# Revit family: QF_ELECTROLUXPROFESSIONAL_1LSNBN_IC64832LF_E
name_source: partatom
category: Attrezzature speciali
units: mm (PartAtom-declared; Revit-internal decimal feet)

## family parameters
Basato su piano di lavoro = No
Condiviso = No
Punto di calcolo locali = No
Quota connettore circolare = Usa diametro
Sempre verticale = Sì
Taglio con vuoti quando caricato = No
Tipo di parte = Normale

## types (14) — shared parameters
Cycle = 50 Hz
Depth Actual = 1110 mm
Height Actual = 1270 mm  [stored 4.16667 ft]
Latent Heat Output = 0.0
Length Actual = 3835 mm
Modello = IC64832LF
Phase = 3
Produttore = Electrolux Professional
Sensible Heat Output = 0.0
URL = www.electroluxprofessional.com
Volts = 400 V
Weight = 1015
zero-valued in all types: Gas KW, Prospetto di default, Steam Pounds per Hour

## per-type parameters (varying)
| type | Descrizione | Item Number | Watts |
| 9882030112 | IRONER CYLINDER IC64832LF LENGTH FOLDING 3170MM ACTIVE EL. CE 400/50/3 6MM SST CYL. SE, DK, FI FEED NOW | 1L0GL8 | 56750 W |
| 9882030140 | IRONER CYLINDER IC64832LF LENGTH FOLDING 3170MM PERFORMANCE EL. CE 400/50/3 DUBIXIUM ML VAC.FEED.TABLE DIAMMS | 1L0GR3 | 56750 W |
| 9882030048 | IRONER CYLINDER IC64832LF LENGTH FOLDING 3170MM EL. CE 400/50/3 6MM SST CYL. FR FEED ALONE VAC.FEED.TABLE DIAMMS | 1LSP2A | 56750 W |
| 9882030007 | IRONER CYLINDER IC64832LF LENGTH FOLDING 3170MM EL. CE 400/50/3 6MM SST CYL. FR FEED NOW FEED ALONE VAC.FEED.TABLE ANTIS | 1LSP74 | 56750 W |
| 9882030125 | IRONER CYLINDER IC64832LF LENGTH FOLDING 3170MM ACTIVE EL. CE 400/50/3 6MM SST CYL. FR FEED NOW | 1L0GMS | 56750 W |
| 9882030057 | IRONER CYLINDER IC64832LF LENGTH FOLDING 3170MM EL. CE 400/50/3 DUBIXIUM FR VAC.FEED.TABLE | 1LSP7M | 56750 W |
| 9882030008 | IRONER CYLINDER IC64832LF LENGTH FOLDING 3170MM EL. CE 400/50/3 6MM SST CYL. FR FEED NOW FEED ALONE VAC.FEED.TABLE ANTIS | 1LSNRU | 56750 W |
| 9882030267 | IRONER CYLINDER IC64832LF LENGTH FOLDING 3170MM EL. CE 400/50/3 DUBIXIUM ML VAC.FEED.TABLE ANTISTATIC DIAMMS | 1LSRJA | 56750 W |
| 9882030303 | IRONER CYLINDER IC64832LF LENGTH FOLDING 3170MM EL. CE 400/50/3 DUBIXIUM SE, DK, FI VAC.FEED.TABLE ANTISTATIC DIAMMS | 1LT66Z | 5675000 W |
| 9882030054 | IRONER CYLINDER IC64832LF LENGTH FOLDING 3170MM EL. CE 400/50/3 DUBIXIUM FR | 1LSP6K | 56750 W |
| 9882030023 | IRONER CYLINDER IC64832LF LENGTH FOLDING 3170MM PERFORMANCE EL. CE 400/50/3 DUBIXIUM FR VAC.FEED.TABLE DIAMMS | 1LA07N | 56750 W |
| 9882030126 | IRONER CYLINDER IC64832LF LENGTH FOLDING 3170MM SUPERIOR EL. CE 400/50/3 DUBIXIUM FR FEED ALONE VAC.FEED.TABLE ANTISTATI | 1L0GMT | 56750 W |
| 9882030022 | IRONER CYLINDER IC64832LF LENGTH FOLDING 3170MM EL. CE 400/50/3 DUBIXIUM FR ANTISTATIC DIAMMS | 1LA07M | 56750 W |
| 9882030139 | IRONER CYLINDER IC64832LF LENGTH FOLDING 3170MM ACTIVE EL. CE 400/50/3 6MM SST CYL. ML FEED NOW | 1L0GR2 | 56750 W |

note: [stored X ft] marks values corroborated as IEEE doubles in the binary element streams (Revit-internal decimal feet)

## geometry (parser evidence)
native form markers: Sweep x11
no freeform markers — native parametric forms only
